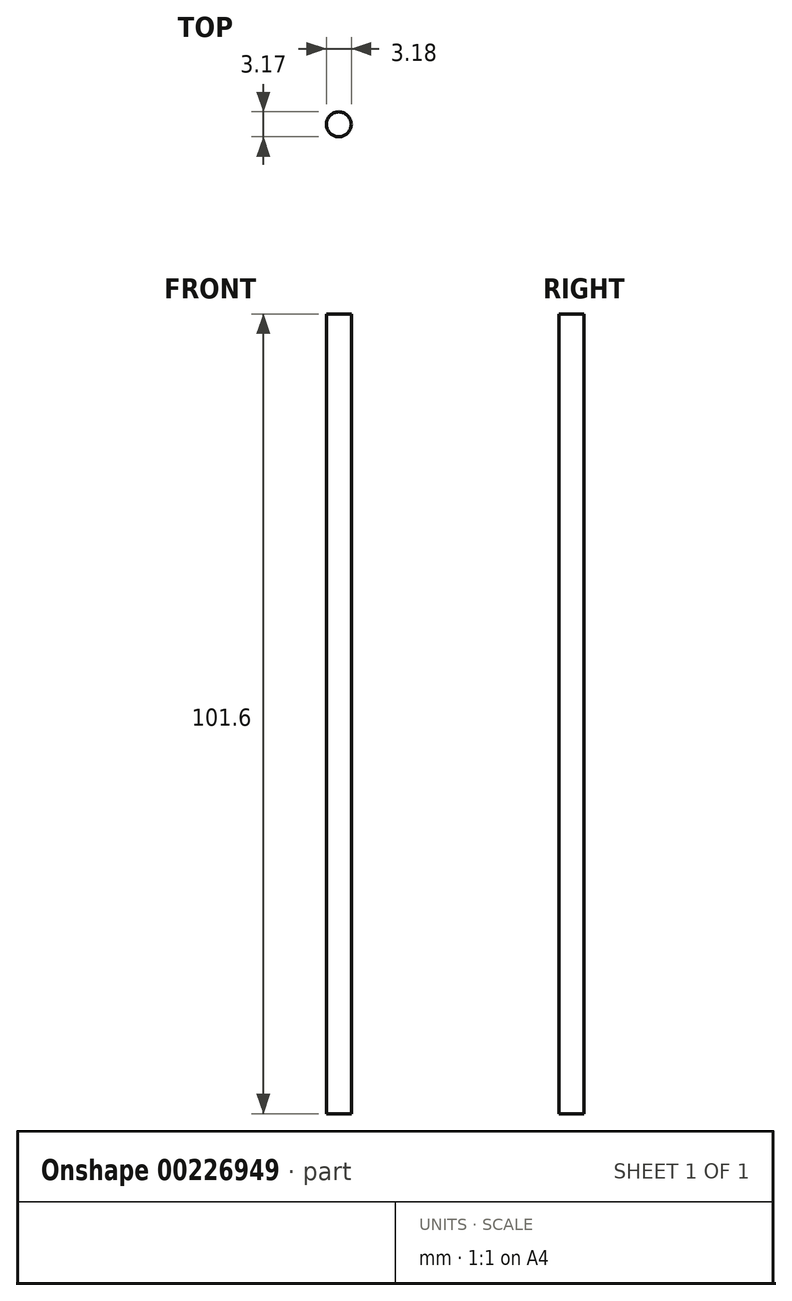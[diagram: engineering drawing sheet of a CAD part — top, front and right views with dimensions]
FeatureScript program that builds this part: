
annotation { "Feature Type Name" : "Feature", "Feature Type Description" : "" }
export const myFeature = defineFeature(function(context is Context, id is Id, definition is map)
    precondition{}
    {
        {
            var Q0;
            Q0=qCreatedBy(makeId("Top.planeOp"),FACE);
            var sketch = newSketch(context, id + "F0", { "sketchPlane" : qUnion([Q0])});
            skCircle(sketch, "E0", {"center": v(-24.2, 37.16) * mm, "radius": 1.59 * mm});
            skSolve(sketch);
        }
        {
            var Q0;
            Q0=makeQuery(id+"F0.imprint","IMPRINT",FACE,{"disambiguationData":[TD([[makeQuery(id+"F0.imprint","IMPRINT",EDGE,{"derivedFrom":sQuery(id+"F0.wireOp",EDGE,"E0")}),1.0]])]});
            extrude(context, id + "F1", {"entities" : qUnion([Q0]), "depth" : 101.6 * mm});
        }
    });
